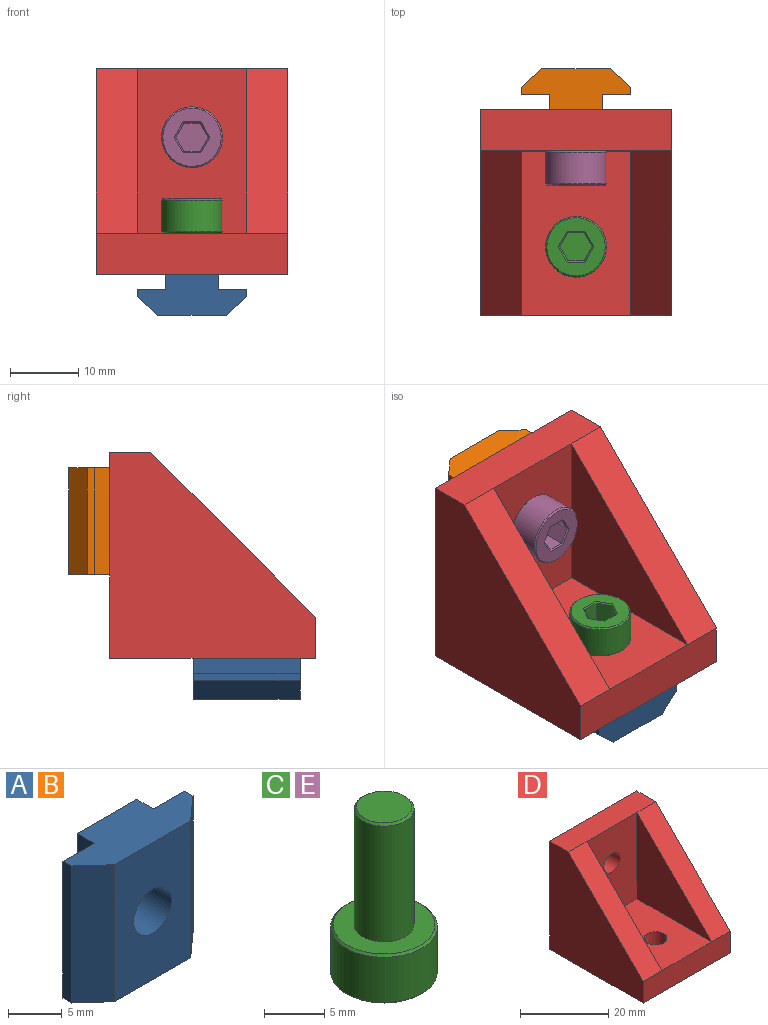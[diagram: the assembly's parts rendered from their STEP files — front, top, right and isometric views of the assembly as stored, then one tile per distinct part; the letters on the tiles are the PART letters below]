
ASSEMBLY  parts=5 mates=4
PART A: 13 faces, bbox 16x6x15.6 mm
  f0: plane 15.6x2.2mm, normal (1,0,0), area 34.3mm2, adj f1,f9,f10,f11
  f1: plane 15.6x7.8mm, normal (0,1,0), area 102mm2, adj f0,f2,f10,f11,f12
  f2: plane 15.6x2.2mm, normal (-1,0,0), area 34.3mm2, adj f1,f3,f10,f11
  f3: plane 15.6x4.1mm, normal (0,1,0), area 64mm2, adj f2,f4,f10,f11
  f4: plane 15.6x1.1mm, normal (-1,0,0), area 17.2mm2, adj f3,f5,f10,f11
  f5: plane 15.6x3mm, normal (-0.67,-0.74,0), area 63mm2, adj f4,f6,f10,f11
  f6: plane 15.6x10mm, normal (0,-1,0), area 136.4mm2, adj f5,f7,f10,f11,f12
  f7: plane 15.6x3mm, normal (0.67,-0.74,0), area 63mm2, adj f6,f8,f10,f11
  f8: plane 15.6x1.1mm, normal (1,0,0), area 17.2mm2, adj f7,f9,f10,f11
  f9: plane 15.6x4.1mm, normal (0,1,0), area 64mm2, adj f0,f8,f10,f11
  f10: plane 16x6mm, normal (0,0,1), area 69.9mm2, adj f0,f1,f2,f3,f4,f5,f6,f7
  f11: plane 16x6mm, normal (0,0,-1), area 69.9mm2, adj f0,f1,f2,f3,f4,f5,f6,f7
  f12: cylinder r=2.5mm len=6mm, axis (0,1,0), area 94.2mm2, adj f1,f6
PART B: same geometry as A
PART C: 21 faces, bbox 8.9x8.9x17 mm
  f0: plane 3.8x2.37mm, normal (0,-1,0), area 9mm2, adj f1,f5,f8,f17
  f1: plane 3.8x2.05mm, normal (-0.87,-0.5,0), area 9mm2, adj f0,f2,f8,f18
  f2: plane 3.8x2.05mm, normal (-0.87,0.5,0), area 9mm2, adj f1,f3,f8,f16
  f3: plane 3.8x2.37mm, normal (0,1,0), area 9mm2, adj f2,f4,f8,f14
  f4: plane 3.8x2.05mm, normal (0.87,0.5,0), area 9mm2, adj f3,f5,f8,f13
  f5: plane 3.8x2.05mm, normal (0.87,-0.5,0), area 9mm2, adj f0,f4,f8,f15
  f6: cylinder r=4.45mm len=8.9mm, axis (0,0,-1), area 128.6mm2, adj f12,f19
  f7: plane 8.5x8.5mm, normal (0,0,-1), area 39.2mm2, adj f13,f14,f15,f16,f17,f18,f19
  f8: plane 4.73x4.1mm, normal (0,0,-1), area 14.6mm2, adj f0,f1,f2,f3,f4,f5
  f9: plane 8.5x8.5mm, normal (0,0,1), area 37.1mm2, adj f10,f12
  f10: cylinder r=2.5mm len=11.8mm, axis (0,0,-1), area 185.4mm2, adj f9,f20
  f11: plane 4.6x4.6mm, normal (0,0,1), area 16.6mm2, adj f20
  f12: cone r=4.25mm half-angle=45deg, axis (0,0,-1), area 7.7mm2, adj f6,f9
  f13: plane 2.25x1.41mm, normal (0.61,0.35,-0.71), area 0.7mm2, adj f4,f7,f14,f15
  f14: plane 2.6x0.2mm, normal (0,0.71,-0.71), area 0.7mm2, adj f3,f7,f13,f16
  f15: plane 2.25x1.41mm, normal (0.61,-0.35,-0.71), area 0.7mm2, adj f5,f7,f13,f17
  f16: plane 2.25x1.41mm, normal (-0.61,0.35,-0.71), area 0.7mm2, adj f2,f7,f14,f18
  f17: plane 2.6x0.2mm, normal (0,-0.71,-0.71), area 0.7mm2, adj f0,f7,f15,f18
  f18: plane 2.25x1.41mm, normal (-0.61,-0.35,-0.71), area 0.7mm2, adj f1,f7,f16,f17
  f19: cone r=4.45mm half-angle=45deg, axis (0,0,1), area 7.7mm2, adj f6,f7
  f20: cone r=2.3mm half-angle=45deg, axis (0,0,-1), area 4.3mm2, adj f10,f11
PART D: 14 faces, bbox 28x30x30 mm
  f0: plane 28x6mm, normal (0,-1,0), area 168mm2, adj f1,f3,f4,f5,f10,f11
  f1: plane 30x30mm, normal (1,0,0), area 612mm2, adj f0,f2,f5,f9,f10
  f2: plane 30x28mm, normal (0,1,0), area 818.8mm2, adj f1,f3,f5,f9,f12
  f3: plane 30x30mm, normal (-1,0,0), area 612mm2, adj f0,f2,f5,f9,f11
  f4: plane 24x16mm, normal (0,0,1), area 362.8mm2, adj f0,f6,f7,f8,f13
  f5: plane 30x28mm, normal (0,0,-1), area 818.8mm2, adj f0,f1,f2,f3,f13
  f6: plane 24x16mm, normal (0,-1,0), area 362.8mm2, adj f4,f7,f8,f9,f12
  f7: plane 24x24mm, normal (-1,0,0), area 288mm2, adj f4,f6,f10
  f8: plane 24x24mm, normal (1,0,0), area 288mm2, adj f4,f6,f11
  f9: plane 28x6mm, normal (0,0,1), area 168mm2, adj f1,f2,f3,f6,f10,f11
  f10: plane 24x24mm, normal (0,-0.71,0.71), area 203.6mm2, adj f0,f1,f7,f9
  f11: plane 24x24mm, normal (0,-0.71,0.71), area 203.6mm2, adj f0,f3,f8,f9
  f12: cylinder r=2.6mm len=6mm, axis (0,-1,0), area 98mm2, adj f2,f6
  f13: cylinder r=2.6mm len=6mm, axis (0,0,1), area 98mm2, adj f4,f5
PART E: same geometry as C
PLACE A rot(axis=(1,0,0),90deg) t=(-42.47,12.54,28.32)mm
PLACE B rot(axis=(1,0,0),180deg) t=(-42.47,-1.23,30.15)mm
PLACE C rot(axis=(0,1,0),180deg) t=(-62.31,-3.34,13.35)mm
PLACE D t=(-47.1,-5.26,2.35)mm
PLACE E rot(axis=(0,0.71,0.71),180deg) t=(-62.31,13.74,14.27)mm
MATE fastened B.f12 <-> E.f6  axis (0,-1,0) through (-95.03,24.74,22.35)mm
MATE fastened E.f6 <-> D.f12  axis (0,1,0) through (-95.03,18.74,22.35)mm
MATE fastened D.f13 <-> C.f6  axis (0,0,1) through (-95.03,4.74,8.35)mm
MATE fastened A.f12 <-> C.f6  axis (0,0,1) through (-95.03,4.74,2.35)mm
